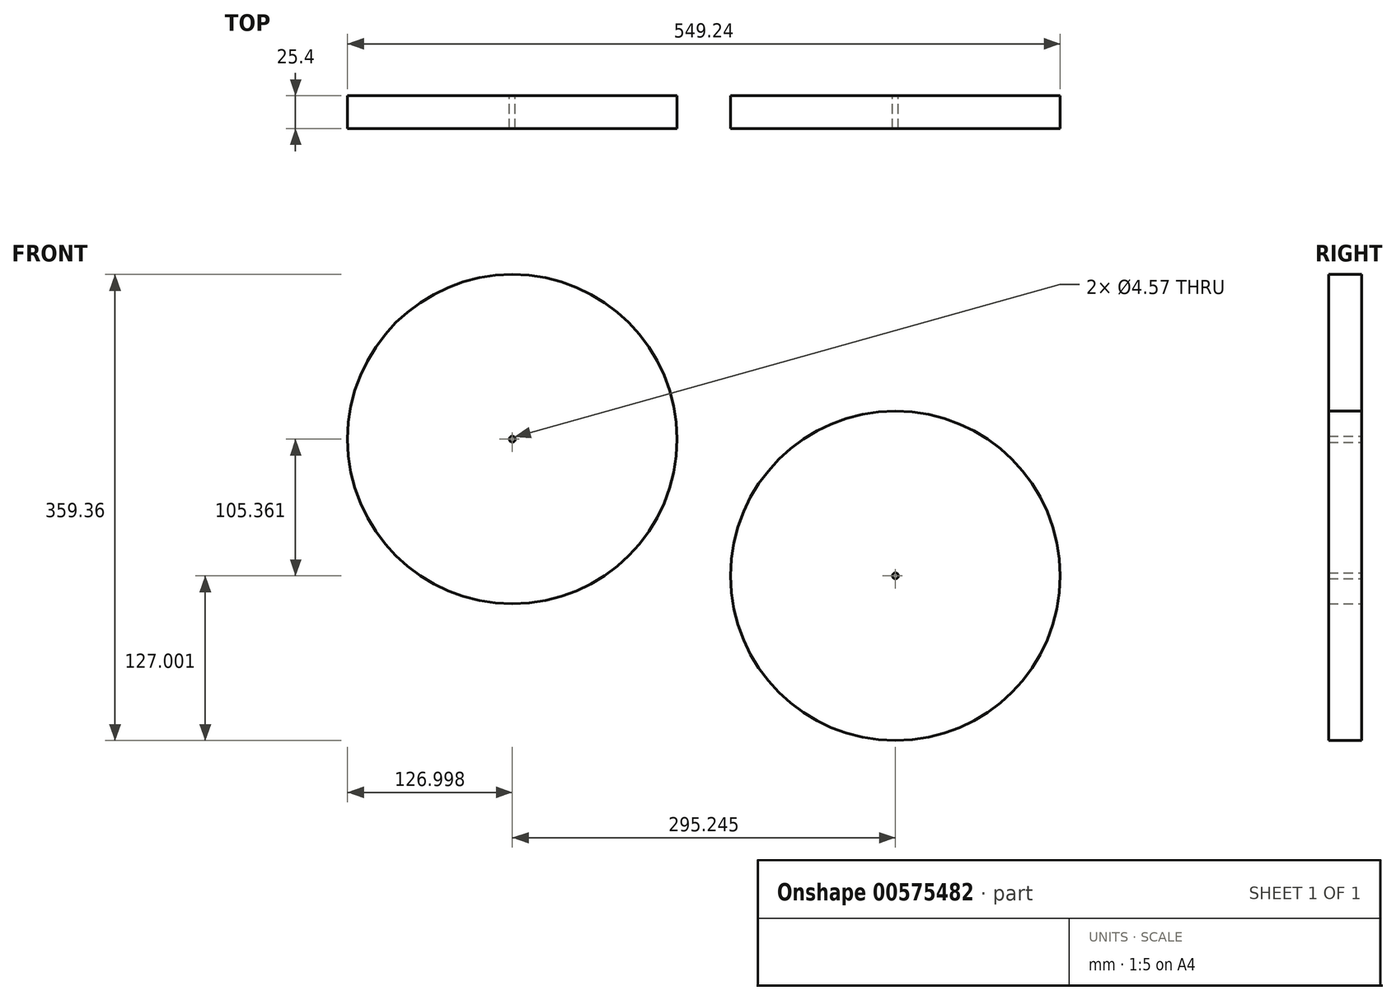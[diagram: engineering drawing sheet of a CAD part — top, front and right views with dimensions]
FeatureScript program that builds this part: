
annotation { "Feature Type Name" : "Feature", "Feature Type Description" : "" }
export const myFeature = defineFeature(function(context is Context, id is Id, definition is map)
    precondition{}
    {
        {
            var Q0;
            Q0=qCreatedBy(makeId("Front.planeOp"),FACE);
            var sketch = newSketch(context, id + "F0", { "sketchPlane" : qUnion([Q0])});
            skCircle(sketch, "E0", {"center": v(-37.43, 51.58) * mm, "radius": 127 * mm});
            skCircle(sketch, "E1", {"center": v(257.81, -53.78) * mm, "radius": 127 * mm});
            skCircle(sketch, "E2", {"center": v(-37.43, 51.58) * mm, "radius": 2.29 * mm});
            skCircle(sketch, "E3", {"center": v(257.81, -53.78) * mm, "radius": 2.29 * mm});
            skSolve(sketch);
        }
        {
            var Q0;
            Q0 = qSketchRegion(id + "F0", true);
            extrude(context, id + "F1", {"entities" : qUnion([Q0]), "depth" : 25.4 * mm, "offsetDistance" : 25.4 * mm});
        }
    });
